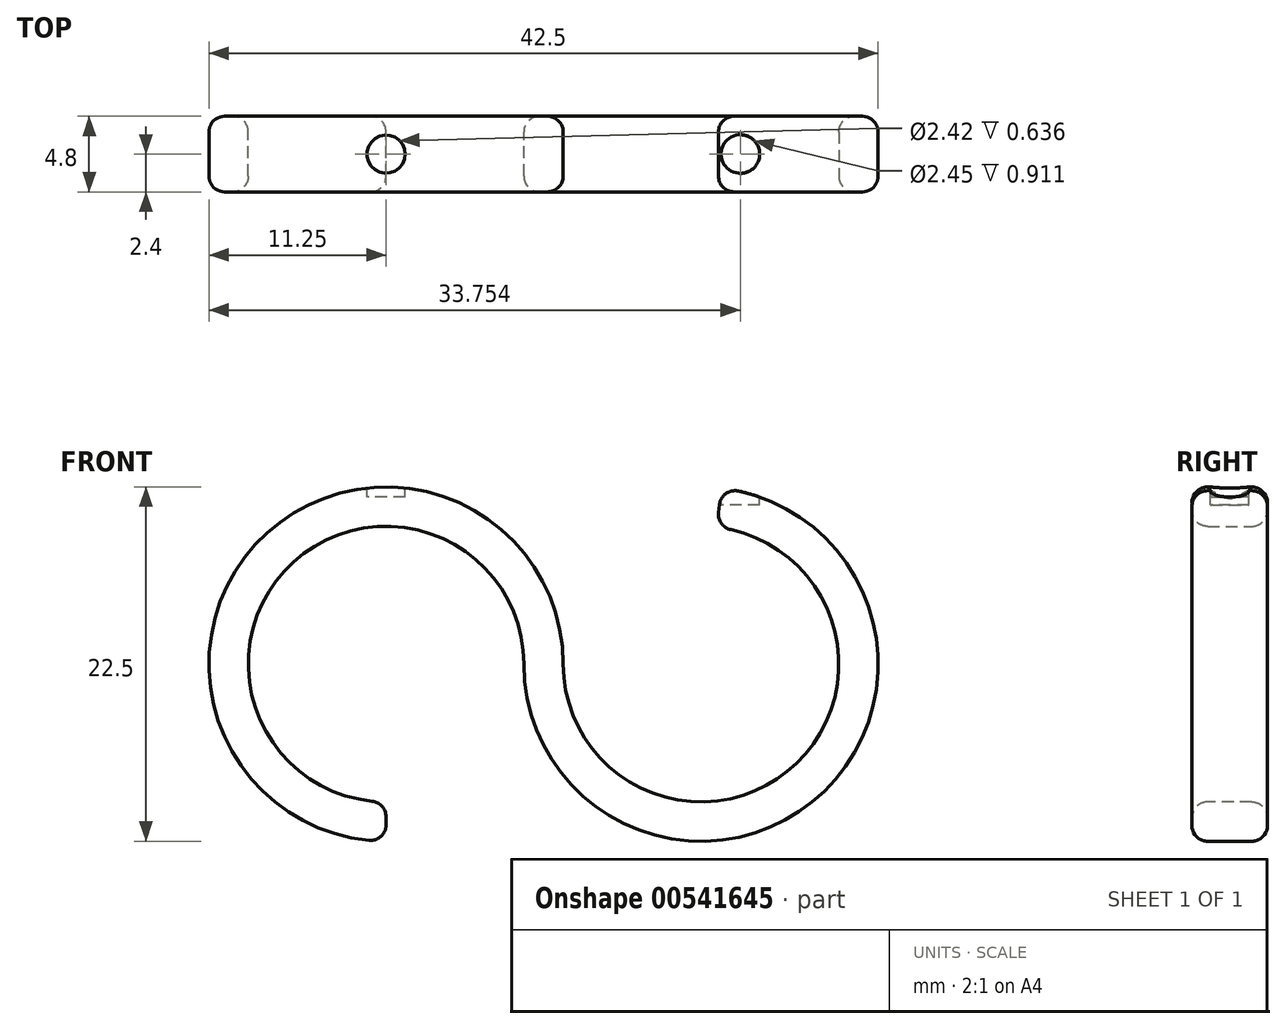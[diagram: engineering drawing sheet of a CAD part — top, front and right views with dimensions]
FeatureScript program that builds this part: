
annotation { "Feature Type Name" : "Feature", "Feature Type Description" : "" }
export const myFeature = defineFeature(function(context is Context, id is Id, definition is map)
    precondition{}
    {
        {
            var Q0;
            Q0=qCreatedBy(makeId("Front.planeOp"),FACE);
            var sketch = newSketch(context, id + "F0", { "sketchPlane" : qUnion([Q0])});
            skArc(sketch, "E0", {"start": v(8.85, -22.2) * mm, "mid": v(-7.43, -19.4) * mm, "end": v(0, -34.16) * mm});
            skArc(sketch, "E1", {"start": v(10.56, -27.77) * mm, "mid": v(27.03, -30.45) * mm, "end": v(18.82, -15.93) * mm});
            skPoint(sketch, "E2", {"position": v(0, -34.16) * mm});
            skFitSpline(sketch, "E3", {"points": [v(8.85, -22.2) * mm, v(10.65, -28.05) * mm], "startDerivative": vector(1.82, -5.84) * mm, "endDerivative": vector(1.82, -5.84) * mm});
            skPoint(sketch, "E4", {"position": v(18.82, -15.93) * mm});
            skSolve(sketch);
        }
        {
            var Q0;
            Q0=qCreatedBy(makeId("Front.planeOp"),FACE);
            var sketch = newSketch(context, id + "F1", { "sketchPlane" : qUnion([Q0])});
            skArc(sketch, "E5", {"start": v(10, -52.27) * mm, "mid": v(-7.07, -45.2) * mm, "end": v(0, -62.27) * mm});
            skArc(sketch, "E6", {"start": v(10, -52.27) * mm, "mid": v(26.65, -59.74) * mm, "end": v(21.15, -42.34) * mm});
            skPoint(sketch, "E7", {"position": v(10, -52.27) * mm});
            skPoint(sketch, "E8", {"position": v(0, -62.27) * mm});
            skPoint(sketch, "E9", {"position": v(21.15, -42.34) * mm});
            skSolve(sketch);
        }
        {
            var Q0;
            Q0=sQuery(id+"F0.wireOp",EDGE,"E0");
            var Q1;
            Q1=sQuery(id+"F0.wireOp",VERTEX,"E2");
            cPlane(context, id + "F2", {"entities" : qUnion([Q0, Q1]), "cplaneType" : CPlaneType.CURVE_POINT, "offset" : 25.4 * mm, "width" : 152.4 * mm, "height" : 152.4 * mm});
        }
        {
            var Q0;
            Q0=qCreatedBy(id+"F2.planeOp",FACE);
            var sketch = newSketch(context, id + "F3", { "sketchPlane" : qUnion([Q0])});
            skLineSegment(sketch, "E10.bottom", {"start": v(-1.4, -61.02) * mm, "end": v(1.4, -61.02) * mm});
            skLineSegment(sketch, "E10.top", {"start": v(-1.4, -63.52) * mm, "end": v(1.4, -63.52) * mm});
            skLineSegment(sketch, "E10.left", {"start": v(-2.4, -62.02) * mm, "end": v(-2.4, -62.52) * mm});
            skLineSegment(sketch, "E10.right", {"start": v(2.4, -62.02) * mm, "end": v(2.4, -62.52) * mm});
            skPoint(sketch, "E11", {"position": v(-2.4, -62.27) * mm});
            skLineSegment(sketch, "E12", {"start": v(-2.4, -62.27) * mm, "end": v(0, -62.27) * mm});
            skPoint(sketch, "E13", {"position": v(0, -61.02) * mm});
            skLineSegment(sketch, "E14", {"start": v(0, -61.02) * mm, "end": v(0, -62.27) * mm});
            skPoint(sketch, "E15.visualSharp", {"position": v(-2.4, -61.02) * mm});
            skArc(sketch, "E15.filletArc", {"start": v(-1.4, -61.02) * mm, "mid": v(-2.1, -61.31) * mm, "end": v(-2.4, -62.02) * mm});
            skArc(sketch, "E16.MirrorCS", {"start": v(-1.4, -63.52) * mm, "mid": v(-2.1, -63.23) * mm, "end": v(-2.4, -62.52) * mm});
            skArc(sketch, "E17.MirrorCS", {"start": v(1.4, -61.02) * mm, "mid": v(2.1, -61.31) * mm, "end": v(2.4, -62.02) * mm});
            skArc(sketch, "E18.MirrorCS", {"start": v(1.4, -63.52) * mm, "mid": v(2.1, -63.23) * mm, "end": v(2.4, -62.52) * mm});
            skPoint(sketch, "E19.orphan", {"position": v(-2.4, -63.52) * mm});
            skPoint(sketch, "E20.orphan", {"position": v(2.4, -61.02) * mm});
            skPoint(sketch, "E21", {"position": v(0, -62.27) * mm});
            skSolve(sketch);
        }
        {
            var Q0;
            Q0=makeQuery(id+"F3.imprint","IMPRINT",FACE,{"disambiguationData":[TD([[makeQuery(id+"F3.imprint","IMPRINT",EDGE,{"derivedFrom":sQuery(id+"F3.wireOp",EDGE,"E10.top")}),1.0]])]});
            var Q1;
            {var subQ1=sQuery(id+"F3.wireOp",EDGE,"E12");Q1=makeQuery(id+"F3.imprint","IMPRINT",FACE,{"disambiguationData":[TD([[makeQuery(id+"F3.imprint","IMPRINT",EDGE,{"derivedFrom":subQ1}),1.0]])]});}
            var Q2;
            Q2=sQuery(id+"F1.wireOp",EDGE,"E5");
            var Q3;
            Q3=sQuery(id+"F1.wireOp",EDGE,"E6");
            sweep(context, id + "F4", {"profiles" : qUnion([Q0, Q1]), "path" : qUnion([Q2, Q3])});
        }
        {
            var Q0;
            Q0=makeQuery(id+"F4.opSweep","CAP_FACE",FACE,{"disambiguationData":[OSD([sQuery(id+"F1.wireOp",VERTEX,"E5.end"),sQuery(id+"F3.wireOp",EDGE,"E10.bottom"),sQuery(id+"F3.wireOp",EDGE,"E10.top"),sQuery(id+"F3.wireOp",EDGE,"E10.left"),sQuery(id+"F3.wireOp",EDGE,"E10.right"),sQuery(id+"F3.wireOp",EDGE,"E15.filletArc"),sQuery(id+"F3.wireOp",EDGE,"E16.MirrorCS"),sQuery(id+"F3.wireOp",EDGE,"E17.MirrorCS"),sQuery(id+"F3.wireOp",EDGE,"E18.MirrorCS")])],"isStart":true});
            var Q1;
            Q1=makeQuery(id+"F4.opSweep","CAP_FACE",FACE,{"disambiguationData":[OSD([sQuery(id+"F1.wireOp",VERTEX,"E6.end"),sQuery(id+"F3.wireOp",EDGE,"E10.bottom"),sQuery(id+"F3.wireOp",EDGE,"E10.top"),sQuery(id+"F3.wireOp",EDGE,"E10.left"),sQuery(id+"F3.wireOp",EDGE,"E10.right"),sQuery(id+"F3.wireOp",EDGE,"E15.filletArc"),sQuery(id+"F3.wireOp",EDGE,"E16.MirrorCS"),sQuery(id+"F3.wireOp",EDGE,"E17.MirrorCS"),sQuery(id+"F3.wireOp",EDGE,"E18.MirrorCS")])],"isStart":false});
            fillet(context, id + "F5", {"entities" : qUnion([Q0, Q1]), "radius" : 1 * mm, "tangentPropagation" : true, "allowEdgeOverflow" : false});
        }
        {
            var Q0;
            Q0=qCreatedBy(makeId("Top.planeOp"),FACE);
            var sketch = newSketch(context, id + "F6", { "sketchPlane" : qUnion([Q0])});
            skCircle(sketch, "E22", {"center": v(0, 0) * mm, "radius": 1.2 * mm});
            skSolve(sketch);
        }
        {
            var Q0;
            Q0=makeQuery(id+"F6.imprint","IMPRINT",FACE,{"disambiguationData":[TD([[makeQuery(id+"F6.imprint","IMPRINT",EDGE,{"derivedFrom":sQuery(id+"F6.wireOp",EDGE,"E22")}),1.0]])]});
            extrude(context, id + "F7", {"entities" : qUnion([Q0]), "operationType" : NewBodyOperationType.REMOVE, "oppositeDirection" : true, "depth" : 41.66 * mm, "offsetDistance" : 25.4 * mm});
        }
        {
            var Q0;
            Q0=qCreatedBy(makeId("Top.planeOp"),FACE);
            var sketch = newSketch(context, id + "F8", { "sketchPlane" : qUnion([Q0])});
            skCircle(sketch, "E23", {"center": v(22.5, 0) * mm, "radius": 1.23 * mm});
            skSolve(sketch);
        }
        {
            var Q0;
            Q0=makeQuery(id+"F8.imprint","IMPRINT",FACE,{"disambiguationData":[TD([[makeQuery(id+"F8.imprint","IMPRINT",EDGE,{"derivedFrom":sQuery(id+"F8.wireOp",EDGE,"E23")}),1.0]])]});
            extrude(context, id + "F9", {"entities" : qUnion([Q0]), "operationType" : NewBodyOperationType.REMOVE, "oppositeDirection" : true, "depth" : 42.16 * mm, "offsetDistance" : 25.4 * mm});
        }
    });
